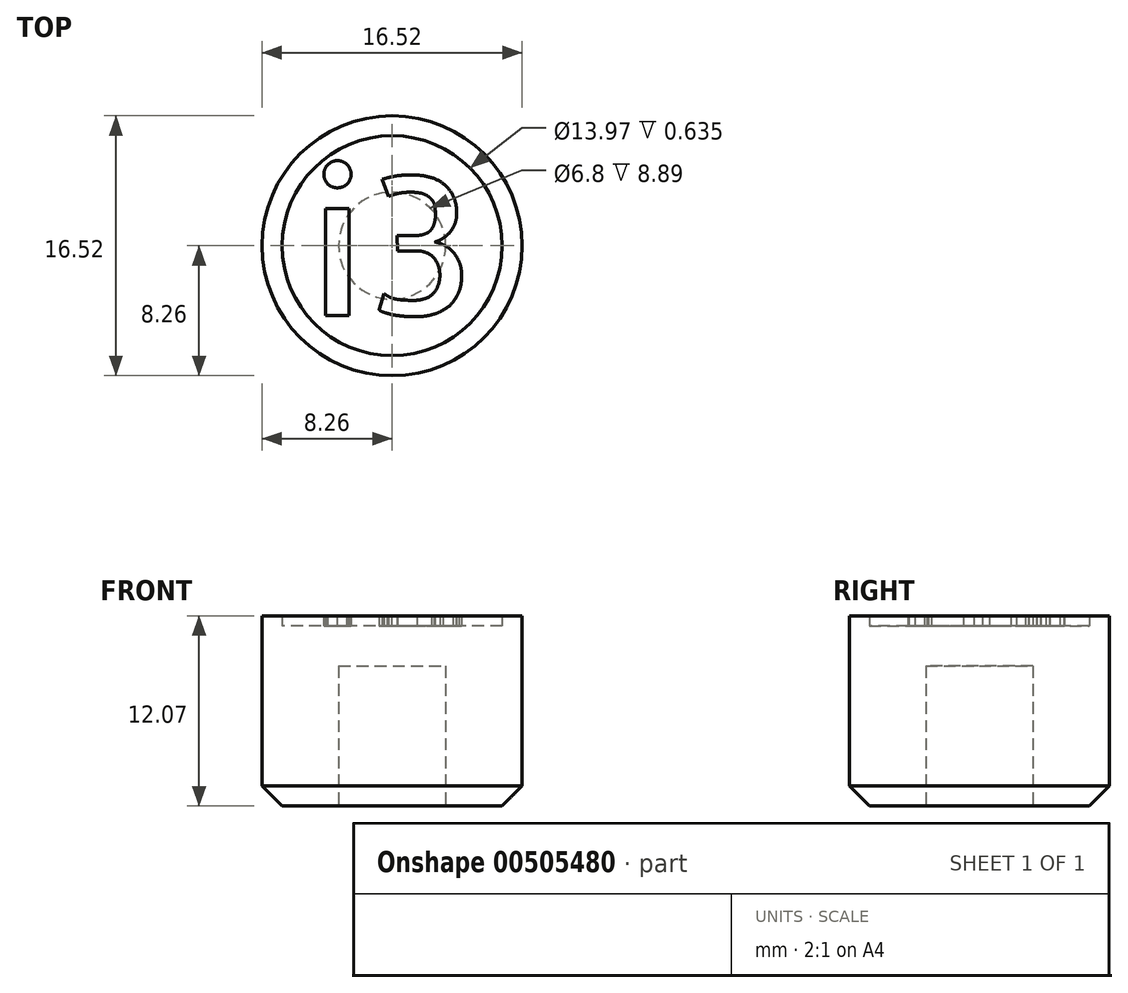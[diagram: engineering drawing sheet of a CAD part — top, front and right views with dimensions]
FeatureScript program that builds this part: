
annotation { "Feature Type Name" : "Feature", "Feature Type Description" : "" }
export const myFeature = defineFeature(function(context is Context, id is Id, definition is map)
    precondition{}
    {
        {
            var Q0;
            Q0=qCreatedBy(makeId("Top.planeOp"),FACE);
            var sketch = newSketch(context, id + "F0", { "sketchPlane" : qUnion([Q0])});
            skCircle(sketch, "E0", {"center": v(0, 0) * mm, "radius": 8.26 * mm});
            skText(sketch, "E1", { "text": "i3", "fontName": "AllertaStencil-Regular.ttf"});
            skCircle(sketch, "E2.0", {"center": v(0, 0) * mm, "radius": 6.99 * mm});
            const initialGuessF0  = {"E1": [-0.00524, -0.00445, 1, 0, 0.0089]};
            skSetInitialGuess(sketch, initialGuessF0);
            skSolve(sketch);
        }
        {
            var Q0;
            Q0=makeQuery(id+"F0.imprint","IMPRINT",FACE,{"disambiguationData":[TD([[makeQuery(id+"F0.imprint","IMPRINT",EDGE,{"derivedFrom":sQuery(id+"F0.wireOp",EDGE,"E1.sketch_text.stroke-12")}),-1.0]])]});
            var Q1;
            Q1=makeQuery(id+"F0.imprint","IMPRINT",FACE,{"disambiguationData":[TD([[makeQuery(id+"F0.imprint","IMPRINT",EDGE,{"derivedFrom":sQuery(id+"F0.wireOp",EDGE,"E1.sketch_text.stroke-0")}),-1.0]])]});
            var Q2;
            Q2=makeQuery(id+"F0.imprint","IMPRINT",FACE,{"disambiguationData":[TD([[makeQuery(id+"F0.imprint","IMPRINT",EDGE,{"derivedFrom":sQuery(id+"F0.wireOp",EDGE,"E1.sketch_text.stroke-4")}),-1.0]])]});
            var Q3;
            Q3=makeQuery(id+"F0.imprint","IMPRINT",FACE,{"disambiguationData":[TD([[makeQuery(id+"F0.imprint","IMPRINT",EDGE,{"derivedFrom":sQuery(id+"F0.wireOp",EDGE,"E0")}),1.0]])]});
            var Q4;
            Q4=makeQuery(id+"F0.imprint","IMPRINT",FACE,{"disambiguationData":[TD([[makeQuery(id+"F0.imprint","IMPRINT",EDGE,{"derivedFrom":sQuery(id+"F0.wireOp",EDGE,"E1.sketch_text.stroke-0")}),1.0]])]});
            extrude(context, id + "F1", {"entities" : qUnion([Q0, Q1, Q2, Q3, Q4]), "oppositeDirection" : true, "depth" : 11.43 * mm});
        }
        {
            var Q0;
            Q0=makeQuery(id+"F0.imprint","IMPRINT",FACE,{"disambiguationData":[TD([[makeQuery(id+"F0.imprint","IMPRINT",EDGE,{"derivedFrom":sQuery(id+"F0.wireOp",EDGE,"E1.sketch_text.stroke-0")}),-1.0]])]});
            var Q1;
            Q1=makeQuery(id+"F0.imprint","IMPRINT",FACE,{"disambiguationData":[TD([[makeQuery(id+"F0.imprint","IMPRINT",EDGE,{"derivedFrom":sQuery(id+"F0.wireOp",EDGE,"E1.sketch_text.stroke-12")}),-1.0]])]});
            var Q2;
            Q2=makeQuery(id+"F0.imprint","IMPRINT",FACE,{"disambiguationData":[TD([[makeQuery(id+"F0.imprint","IMPRINT",EDGE,{"derivedFrom":sQuery(id+"F0.wireOp",EDGE,"E1.sketch_text.stroke-4")}),-1.0]])]});
            var Q3;
            Q3=makeQuery(id+"F0.imprint","IMPRINT",FACE,{"disambiguationData":[TD([[makeQuery(id+"F0.imprint","IMPRINT",EDGE,{"derivedFrom":sQuery(id+"F0.wireOp",EDGE,"E0")}),1.0]])]});
            extrude(context, id + "F2", {"entities" : qUnion([Q0, Q1, Q2, Q3]), "operationType" : NewBodyOperationType.ADD, "depth" : 0.64 * mm});
        }
        {
            var Q0;
            Q0=makeQuery(id+"F1.opExtrude","CAP_FACE",FACE,{"disambiguationData":[OSD([sQuery(id+"F0.wireOp",EDGE,"E0")])],"isStart":false});
            var sketch = newSketch(context, id + "F3", { "sketchPlane" : qUnion([Q0])});
            skPoint(sketch, "E3", {"position": v(0, 0) * mm});
            skCircle(sketch, "E4", {"center": v(0, 0) * mm, "radius": 3.4 * mm});
            skSolve(sketch);
        }
        {
            var Q0;
            Q0=makeQuery(id+"F3.imprint","IMPRINT",FACE,{"disambiguationData":[TD([[makeQuery(id+"F3.imprint","IMPRINT",EDGE,{"derivedFrom":sQuery(id+"F3.wireOp",EDGE,"E4")}),1.0]])]});
            extrude(context, id + "F4", {"entities" : qUnion([Q0]), "operationType" : NewBodyOperationType.REMOVE, "oppositeDirection" : true, "depth" : 8.9 * mm});
        }
        {
            var Q0;
            Q0=makeQuery(id+"F1.opExtrude","CAP_EDGE",EDGE,{"disambiguationData":[OSD([sQuery(id+"F0.wireOp",EDGE,"E0")])],"isStart":false});
            chamfer(context, id + "F5", {"entities" : qUnion([Q0]), "width" : 1.27 * mm, "tangentPropagation" : true});
        }
    });
